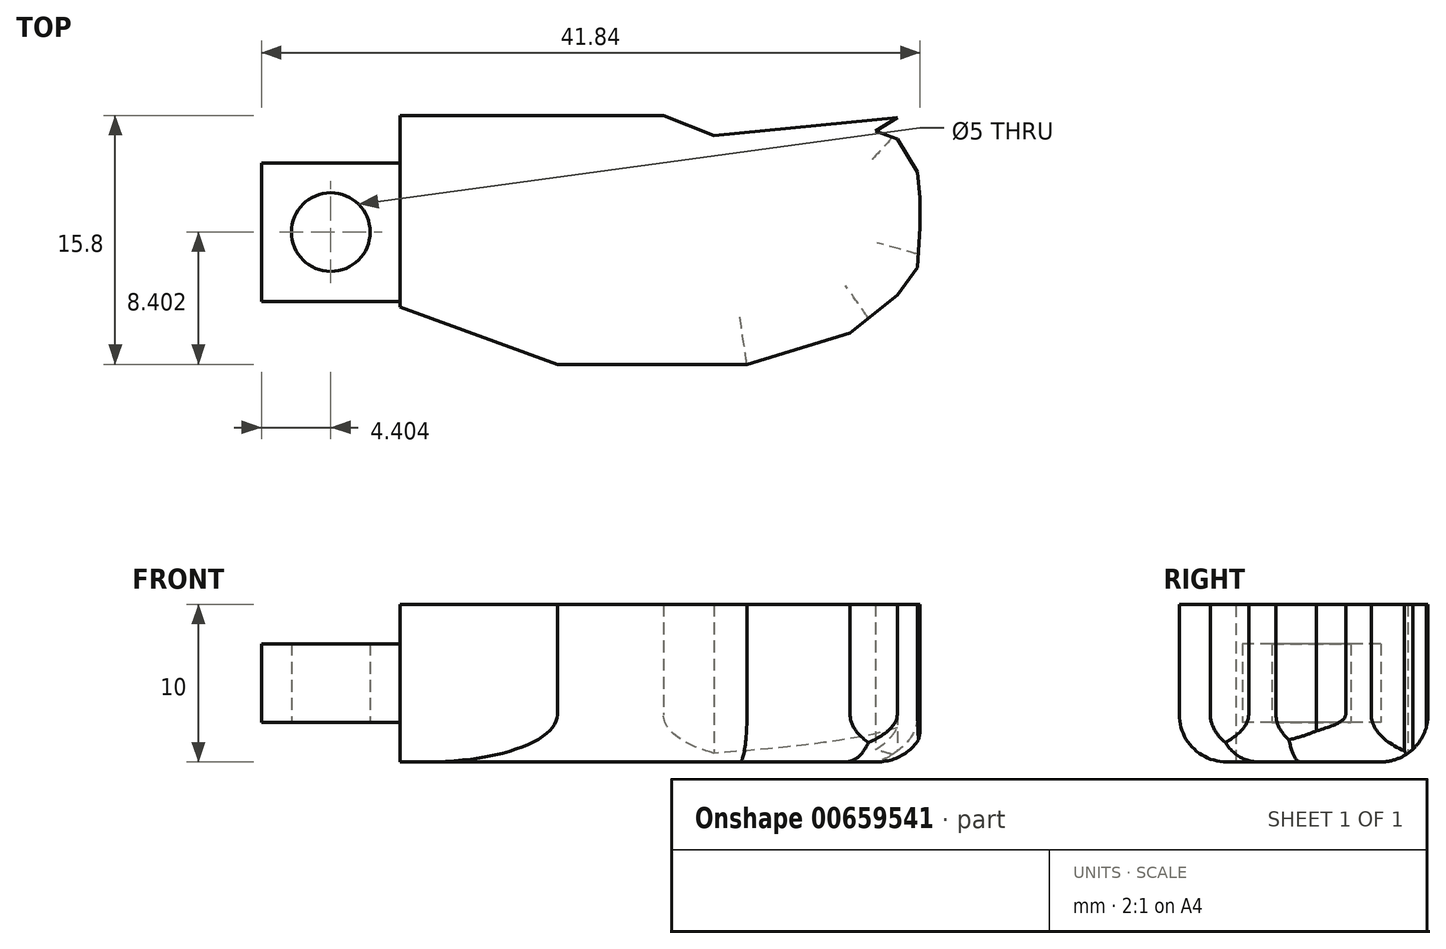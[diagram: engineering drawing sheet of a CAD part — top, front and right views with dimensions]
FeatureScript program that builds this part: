
annotation { "Feature Type Name" : "Feature", "Feature Type Description" : "" }
export const myFeature = defineFeature(function(context is Context, id is Id, definition is map)
    precondition{}
    {
        {
            var Q0;
            Q0=qCreatedBy(makeId("Top.planeOp"),FACE);
            var sketch = newSketch(context, id + "F0", { "sketchPlane" : qUnion([Q0])});
            skLineSegment(sketch, "E0", {"start": v(0, 14.35) * mm, "end": v(10.72, 14.35) * mm});
            skLineSegment(sketch, "E1", {"start": v(10.72, 14.35) * mm, "end": v(13.93, 13.08) * mm});
            skLineSegment(sketch, "E2", {"start": v(13.93, 13.08) * mm, "end": v(25.58, 14.23) * mm});
            skLineSegment(sketch, "E3", {"start": v(25.58, 14.23) * mm, "end": v(24.18, 13.38) * mm});
            skLineSegment(sketch, "E4", {"start": v(24.18, 13.38) * mm, "end": v(25.58, 12.87) * mm});
            skLineSegment(sketch, "E5", {"start": v(25.58, 12.87) * mm, "end": v(26.87, 10.75) * mm});
            skLineSegment(sketch, "E6", {"start": v(26.87, 10.75) * mm, "end": v(27.03, 9.12) * mm});
            skLineSegment(sketch, "E7", {"start": v(27.03, 9.12) * mm, "end": v(27.03, 7.27) * mm});
            skLineSegment(sketch, "E8", {"start": v(27.03, 7.27) * mm, "end": v(26.87, 4.7) * mm});
            skLineSegment(sketch, "E9", {"start": v(26.87, 4.7) * mm, "end": v(25.58, 2.97) * mm});
            skLineSegment(sketch, "E10", {"start": v(25.58, 2.97) * mm, "end": v(22.58, 0.53) * mm});
            skLineSegment(sketch, "E11", {"start": v(22.58, 0.53) * mm, "end": v(16.02, -1.45) * mm});
            skLineSegment(sketch, "E12", {"start": v(16.02, -1.45) * mm, "end": v(0, -1.45) * mm});
            skLineSegment(sketch, "E13", {"start": v(0, 14.35) * mm, "end": v(-6, 14.35) * mm});
            skLineSegment(sketch, "E14", {"start": v(-6, 14.35) * mm, "end": v(-6, 11.35) * mm});
            skLineSegment(sketch, "E15", {"start": v(-6, -1.45) * mm, "end": v(0, -1.45) * mm});
            skLineSegment(sketch, "E16.bottom", {"start": v(-6, 11.35) * mm, "end": v(-14.8, 11.35) * mm});
            skLineSegment(sketch, "E16.top", {"start": v(-6, 2.55) * mm, "end": v(-14.8, 2.55) * mm});
            skLineSegment(sketch, "E16.right", {"start": v(-14.8, 11.35) * mm, "end": v(-14.8, 2.55) * mm});
            skLineSegment(sketch, "E17.trimOffspring", {"start": v(-6, 2.55) * mm, "end": v(-6, -1.45) * mm});
            skCircle(sketch, "E18", {"center": v(-10.4, 6.95) * mm, "radius": 2.5 * mm});
            skPoint(sketch, "E18.centerSnap0", {"position": v(-10.4, 11.35) * mm});
            skPoint(sketch, "E18.centerSnap1", {"position": v(-14.8, 6.95) * mm});
            skSolve(sketch);
        }
        {
            var Q0;
            Q0=makeQuery(id+"F0.imprint","IMPRINT",FACE,{"disambiguationData":[TD([[makeQuery(id+"F0.imprint","IMPRINT",EDGE,{"derivedFrom":sQuery(id+"F0.wireOp",EDGE,"E0")}),-1.0]])]});
            extrude(context, id + "F1", {"entities" : qUnion([Q0]), "depth" : 10 * mm, "offsetDistance" : 25 * mm});
        }
        {
            var Q0;
            Q0=makeQuery(id+"F1.opExtrude","CAP_FACE",FACE,{"disambiguationData":[OSD([sQuery(id+"F0.wireOp",EDGE,"E0"),sQuery(id+"F0.wireOp",EDGE,"E1"),sQuery(id+"F0.wireOp",EDGE,"E2"),sQuery(id+"F0.wireOp",EDGE,"E3"),sQuery(id+"F0.wireOp",EDGE,"E4"),sQuery(id+"F0.wireOp",EDGE,"E5"),sQuery(id+"F0.wireOp",EDGE,"E6"),sQuery(id+"F0.wireOp",EDGE,"E7"),sQuery(id+"F0.wireOp",EDGE,"E8"),sQuery(id+"F0.wireOp",EDGE,"E9"),sQuery(id+"F0.wireOp",EDGE,"E10"),sQuery(id+"F0.wireOp",EDGE,"E11"),sQuery(id+"F0.wireOp",EDGE,"E12"),sQuery(id+"F0.wireOp",EDGE,"E13"),sQuery(id+"F0.wireOp",EDGE,"E14"),sQuery(id+"F0.wireOp",EDGE,"E15"),sQuery(id+"F0.wireOp",EDGE,"E16.bottom"),sQuery(id+"F0.wireOp",EDGE,"E16.top"),sQuery(id+"F0.wireOp",EDGE,"E16.right"),sQuery(id+"F0.wireOp",EDGE,"E17.trimOffspring"),sQuery(id+"F0.wireOp",EDGE,"E18")])],"isStart":false});
            var sketch = newSketch(context, id + "F2", { "sketchPlane" : qUnion([Q0])});
            skLineSegment(sketch, "E19.bottom", {"start": v(-21.72, 12.8) * mm, "end": v(-6, 12.8) * mm});
            skLineSegment(sketch, "E19.top", {"start": v(-21.72, 0) * mm, "end": v(-6, 0) * mm});
            skLineSegment(sketch, "E19.left", {"start": v(-21.72, 12.8) * mm, "end": v(-21.72, 0) * mm});
            skLineSegment(sketch, "E19.right", {"start": v(-6, 12.8) * mm, "end": v(-6, 0) * mm});
            skSolve(sketch);
        }
        {
            var Q0;
            {var subQ1=makeQuery(id+"F1.opExtrude","CAP_EDGE",EDGE,{"disambiguationData":[OSD([sQuery(id+"F0.wireOp",EDGE,"E16.bottom")])],"isStart":false});Q0=makeQuery(id+"F2.imprint","IMPRINT",FACE,{"disambiguationData":[TD([[makeQuery(id+"F2.imprint","IMPRINT",EDGE,{"derivedFrom":subQ1}),1.0]])]});}
            extrude(context, id + "F3", {"entities" : qUnion([Q0]), "operationType" : NewBodyOperationType.REMOVE, "oppositeDirection" : true, "depth" : 2.5 * mm, "offsetDistance" : 25 * mm});
        }
        {
            var Q0;
            Q0=makeQuery(id+"F1.opExtrude","CAP_FACE",FACE,{"disambiguationData":[OSD([sQuery(id+"F0.wireOp",EDGE,"E0"),sQuery(id+"F0.wireOp",EDGE,"E1"),sQuery(id+"F0.wireOp",EDGE,"E2"),sQuery(id+"F0.wireOp",EDGE,"E3"),sQuery(id+"F0.wireOp",EDGE,"E4"),sQuery(id+"F0.wireOp",EDGE,"E5"),sQuery(id+"F0.wireOp",EDGE,"E6"),sQuery(id+"F0.wireOp",EDGE,"E7"),sQuery(id+"F0.wireOp",EDGE,"E8"),sQuery(id+"F0.wireOp",EDGE,"E9"),sQuery(id+"F0.wireOp",EDGE,"E10"),sQuery(id+"F0.wireOp",EDGE,"E11"),sQuery(id+"F0.wireOp",EDGE,"E12"),sQuery(id+"F0.wireOp",EDGE,"E13"),sQuery(id+"F0.wireOp",EDGE,"E14"),sQuery(id+"F0.wireOp",EDGE,"E15"),sQuery(id+"F0.wireOp",EDGE,"E16.bottom"),sQuery(id+"F0.wireOp",EDGE,"E16.top"),sQuery(id+"F0.wireOp",EDGE,"E16.right"),sQuery(id+"F0.wireOp",EDGE,"E17.trimOffspring"),sQuery(id+"F0.wireOp",EDGE,"E18")])],"isStart":true});
            var sketch = newSketch(context, id + "F4", { "sketchPlane" : qUnion([Q0])});
            skLineSegment(sketch, "E20", {"start": v(-6, -2.55) * mm, "end": v(-6, -11.35) * mm});
            skSolve(sketch);
        }
        {
            var Q0;
            Q0=makeQuery(id+"F4.imprint","IMPRINT",FACE,{"disambiguationData":[TD([[makeQuery(id+"F4.imprint","IMPRINT",EDGE,{"derivedFrom":sQuery(id+"F4.wireOp",EDGE,"E20")}),-1.0]])]});
            extrude(context, id + "F5", {"entities" : qUnion([Q0]), "operationType" : NewBodyOperationType.REMOVE, "oppositeDirection" : true, "depth" : 2.5 * mm, "offsetDistance" : 25 * mm});
        }
        {
            var Q0;
            Q0=makeQuery(id+"F1.opExtrude","CAP_EDGE",EDGE,{"disambiguationData":[OSD([sQuery(id+"F0.wireOp",EDGE,"E0"),sQuery(id+"F0.wireOp",EDGE,"E13")])],"isStart":true});
            var Q1;
            Q1=makeQuery(id+"F1.opExtrude","CAP_EDGE",EDGE,{"disambiguationData":[OSD([sQuery(id+"F0.wireOp",EDGE,"E6")])],"isStart":true});
            var Q2;
            Q2=makeQuery(id+"F1.opExtrude","CAP_EDGE",EDGE,{"disambiguationData":[OSD([sQuery(id+"F0.wireOp",EDGE,"E11")])],"isStart":true});
            var Q3;
            Q3=makeQuery(id+"F1.opExtrude","CAP_EDGE",EDGE,{"disambiguationData":[OSD([sQuery(id+"F0.wireOp",EDGE,"E12"),sQuery(id+"F0.wireOp",EDGE,"E15")])],"isStart":true});
            var Q4;
            Q4=makeQuery(id+"F1.opExtrude","CAP_EDGE",EDGE,{"disambiguationData":[OSD([sQuery(id+"F0.wireOp",EDGE,"E9")])],"isStart":true});
            fillet(context, id + "F6", {"entities" : qUnion([Q0, Q1, Q2, Q3, Q4]), "radius" : 3 * mm, "tangentPropagation" : true, "allowEdgeOverflow" : false});
        }
        {
            var Q0;
            Q0=makeQuery(id+"F1.opExtrude","SWEPT_EDGE",EDGE,{"disambiguationData":[OSD([sQuery(id+"F0.wireOp",EDGE,"E15"),sQuery(id+"F0.wireOp",EDGE,"E17.trimOffspring")])]});
            chamfer(context, id + "F7", {"entities" : qUnion([Q0]), "chamferType" : ChamferType.OFFSET_ANGLE, "width" : 10 * mm, "oppositeDirection" : false, "angle" : 20 * degree});
        }
    });
